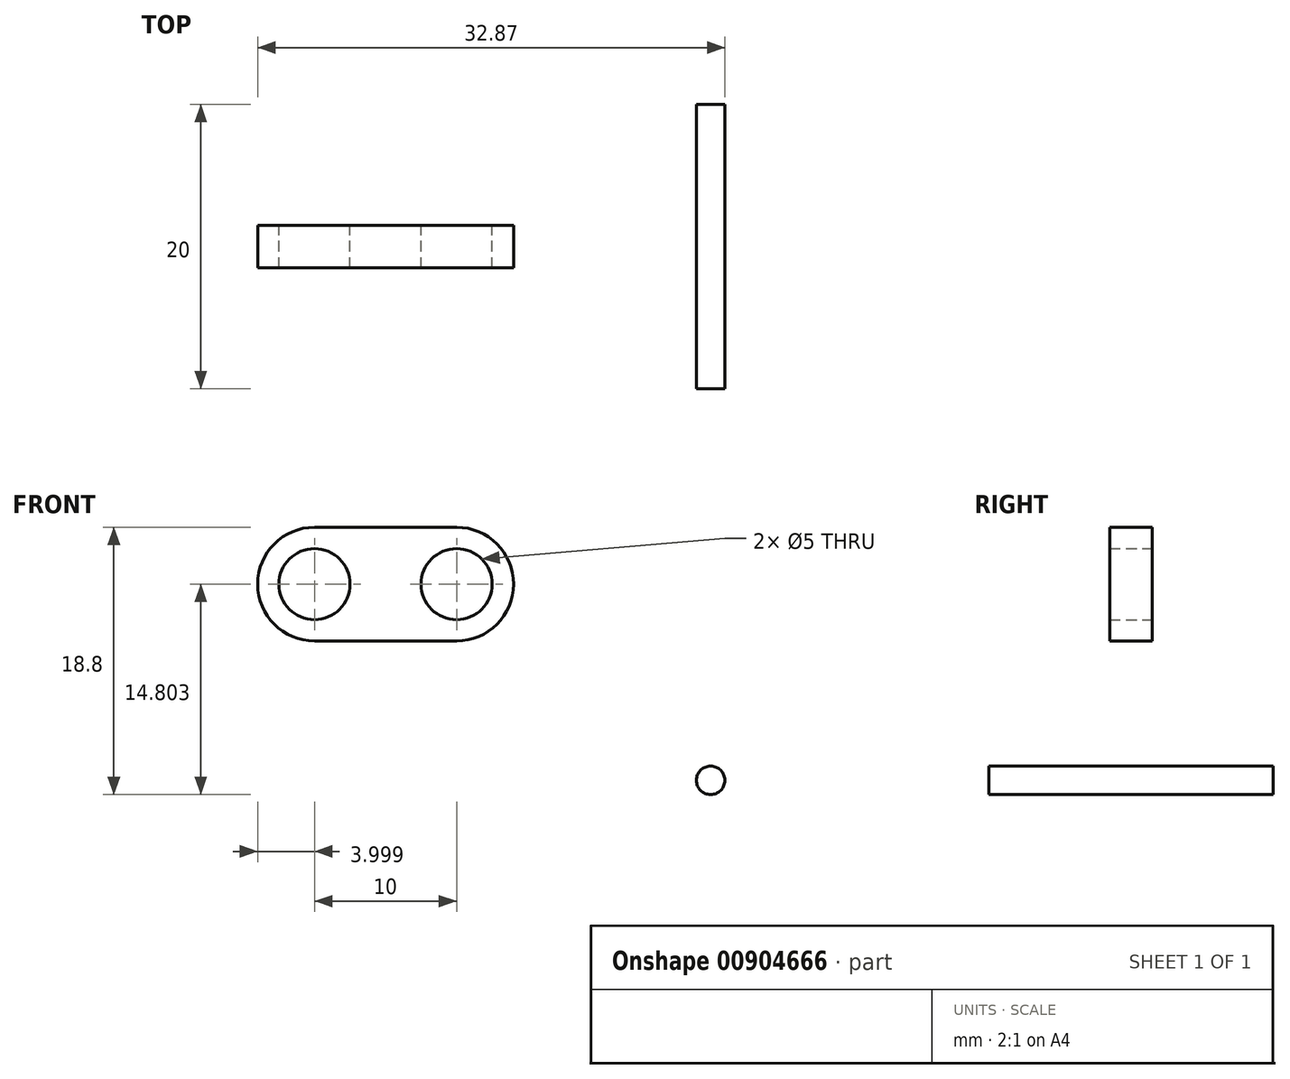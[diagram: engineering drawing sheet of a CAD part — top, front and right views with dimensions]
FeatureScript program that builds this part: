
annotation { "Feature Type Name" : "Feature", "Feature Type Description" : "" }
export const myFeature = defineFeature(function(context is Context, id is Id, definition is map)
    precondition{}
    {
        {
            var Q0;
            Q0=qCreatedBy(makeId("Front.planeOp"),FACE);
            var sketch = newSketch(context, id + "F0", { "sketchPlane" : qUnion([Q0])});
            skLineSegment(sketch, "E0.bottom", {"start": v(-27.87, 9.8) * mm, "end": v(-17.87, 9.8) * mm});
            skLineSegment(sketch, "E0.top", {"start": v(-27.87, 17.8) * mm, "end": v(-17.87, 17.8) * mm});
            skLineSegment(sketch, "E0.left", {"start": v(-27.87, 9.8) * mm, "end": v(-27.87, 17.8) * mm});
            skLineSegment(sketch, "E0.right", {"start": v(-17.87, 9.8) * mm, "end": v(-17.87, 17.8) * mm});
            skArc(sketch, "E1", {"start": v(-27.87, 17.8) * mm, "mid": v(-31.87, 13.8) * mm, "end": v(-27.87, 9.8) * mm});
            skArc(sketch, "E2", {"start": v(-17.87, 9.8) * mm, "mid": v(-13.87, 13.8) * mm, "end": v(-17.87, 17.8) * mm});
            skCircle(sketch, "E3", {"center": v(-17.87, 13.8) * mm, "radius": 2.5 * mm});
            skCircle(sketch, "E4", {"center": v(-27.87, 13.8) * mm, "radius": 2.5 * mm});
            skSolve(sketch);
        }
        {
            var Q0;
            {var subQ5=sQuery(id+"F0.wireOp",EDGE,"E0.bottom");Q0=makeQuery(id+"F0.imprint","IMPRINT",FACE,{"disambiguationData":[TD([[makeQuery(id+"F0.imprint","IMPRINT",EDGE,{"derivedFrom":subQ5}),1.0]])]});}
            var Q1;
            {var subQ0=sQuery(id+"F0.wireOp",EDGE,"E2");Q1=makeQuery(id+"F0.imprint","IMPRINT",FACE,{"disambiguationData":[TD([[makeQuery(id+"F0.imprint","IMPRINT",EDGE,{"derivedFrom":subQ0}),1.0]])]});}
            var Q2;
            {var subQ0=sQuery(id+"F0.wireOp",EDGE,"E1");Q2=makeQuery(id+"F0.imprint","IMPRINT",FACE,{"disambiguationData":[TD([[makeQuery(id+"F0.imprint","IMPRINT",EDGE,{"derivedFrom":subQ0}),1.0]])]});}
            extrude(context, id + "F1", {"entities" : qUnion([Q0, Q1, Q2]), "endBound" : BoundingType.SYMMETRIC, "depth" : 3 * mm, "offsetDistance" : 25 * mm});
        }
        {
            var Q0;
            Q0=qCreatedBy(makeId("Front.planeOp"),FACE);
            var sketch = newSketch(context, id + "F2", { "sketchPlane" : qUnion([Q0])});
            skCircle(sketch, "E5", {"center": v(0, 0) * mm, "radius": 1 * mm});
            skSolve(sketch);
        }
        {
            var Q0;
            Q0=makeQuery(id+"F2.imprint","IMPRINT",FACE,{"disambiguationData":[TD([[makeQuery(id+"F2.imprint","IMPRINT",EDGE,{"derivedFrom":sQuery(id+"F2.wireOp",EDGE,"E5")}),1.0]])]});
            extrude(context, id + "F3", {"entities" : qUnion([Q0]), "endBound" : BoundingType.SYMMETRIC, "depth" : 20 * mm, "offsetDistance" : 25 * mm});
        }
    });
